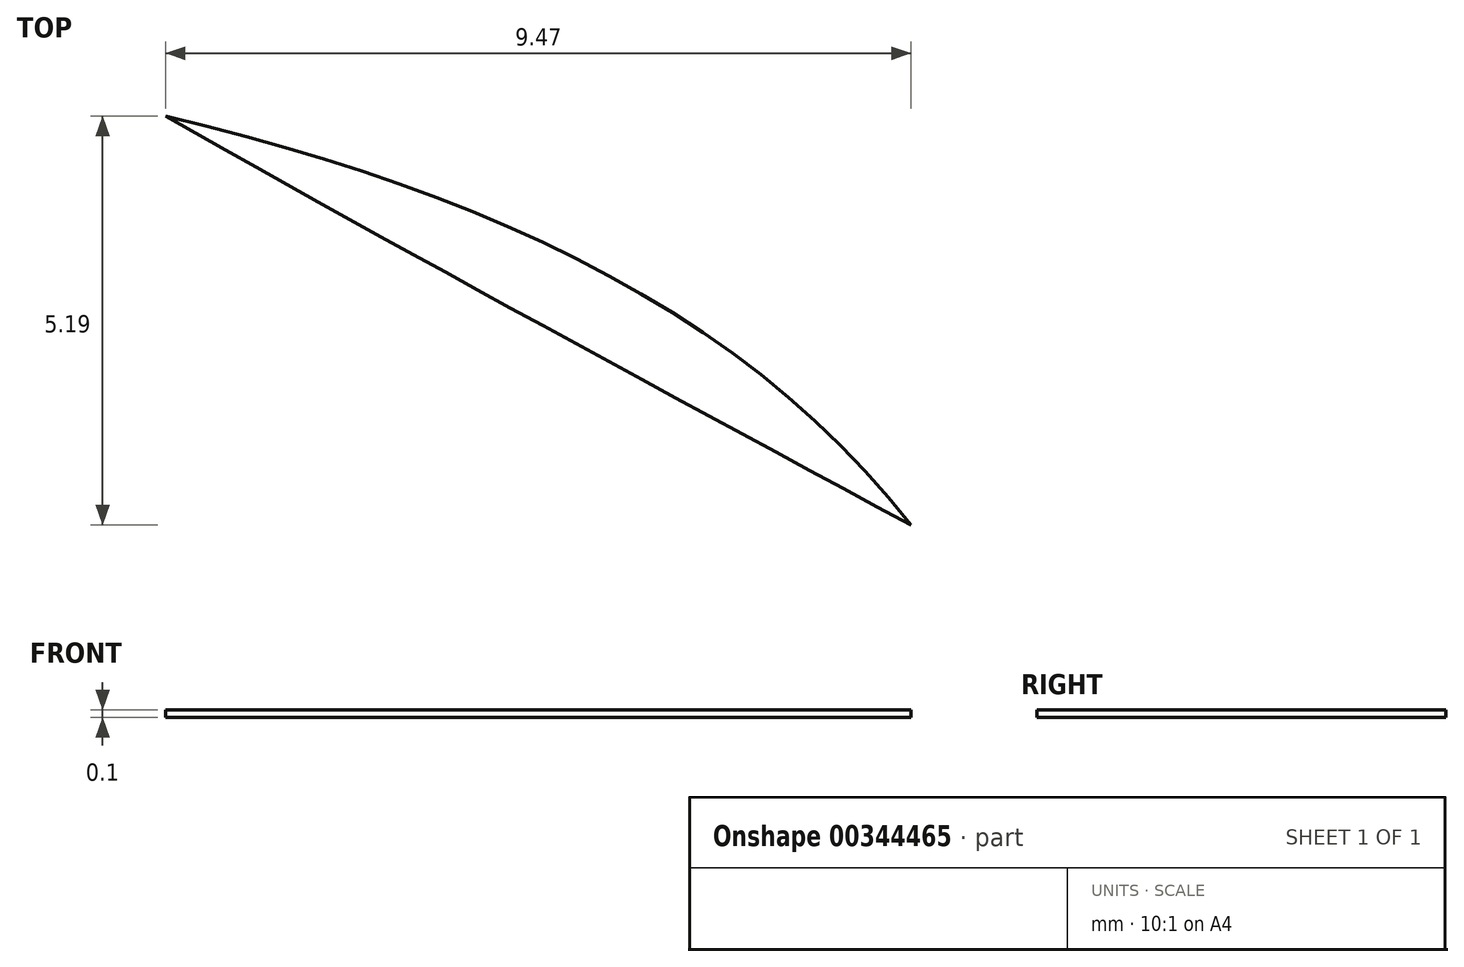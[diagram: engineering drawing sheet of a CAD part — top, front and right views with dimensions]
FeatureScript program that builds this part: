
annotation { "Feature Type Name" : "Feature", "Feature Type Description" : "" }
export const myFeature = defineFeature(function(context is Context, id is Id, definition is map)
    precondition{}
    {
        {
            var Q0;
            Q0=qCreatedBy(makeId("Top.planeOp"),FACE);
            var sketch = newSketch(context, id + "F0", { "sketchPlane" : qUnion([Q0])});
            skCircle(sketch, "E0", {"center": v(-15.45, 15.45) * mm, "radius": 1.5 * mm});
            skCircle(sketch, "E1.MirrorC", {"center": v(15.45, 15.45) * mm, "radius": 1.5 * mm});
            skCircle(sketch, "E2.MirrorC", {"center": v(-15.45, -15.45) * mm, "radius": 1.5 * mm});
            skCircle(sketch, "E3.MirrorC", {"center": v(15.45, -15.45) * mm, "radius": 1.5 * mm});
            skFitSpline(sketch, "E4", {"points": [v(-18, 21.97) * mm, v(-40.78, 23.07) * mm, v(-21.8, 10.59) * mm], "startDerivative": vector(-66.4, 9) * mm, "endDerivative": vector(58.84, -31.77) * mm});
            skFitSpline(sketch, "E5", {"points": [v(-20.03, -19.63) * mm, v(-30, -40.14) * mm, v(-11, -27.53) * mm], "startDerivative": vector(-34.44, -57.57) * mm, "endDerivative": vector(52.5, 41.76) * mm});
            skFitSpline(sketch, "E6", {"points": [v(-20.03, -19.63) * mm, v(-21.8, 10.59) * mm, v(-42.63, 17.36) * mm], "startDerivative": vector(8.08, 67.05) * mm, "endDerivative": vector(-54.98, 5.27) * mm});
            skPoint(sketch, "E7.orphan", {"position": v(-38.92, 28.77) * mm});
            skPoint(sketch, "E8.start.orphan", {"position": v(-21.8, 0) * mm});
            skPoint(sketch, "E9.orphan", {"position": v(-34.52, -36.18) * mm});
            skFitSpline(sketch, "E10", {"points": [v(-18, 21.97) * mm, v(-4.5, 47) * mm, v(0, 47) * mm, v(4.5, 47) * mm, v(18, 21.97) * mm], "startDerivative": vector(39.93, 96.92) * mm, "endDerivative": vector(39.93, -96.92) * mm});
            skPoint(sketch, "E11.start.orphan", {"position": v(-9, 47) * mm});
            skPoint(sketch, "E12.MirrorCS.start.orphan", {"position": v(9, 47) * mm});
            skPoint(sketch, "E13.MirrorP", {"position": v(34.52, -36.18) * mm});
            skFitSpline(sketch, "E14.MirrorCS", {"points": [v(18, 21.97) * mm, v(4.5, 47) * mm, v(0, 47) * mm, v(-4.5, 47) * mm, v(-18, 21.97) * mm], "startDerivative": vector(-39.93, 96.92) * mm, "endDerivative": vector(-39.93, -96.92) * mm});
            skFitSpline(sketch, "E15.MirrorCS", {"points": [v(18, 21.97) * mm, v(40.78, 23.07) * mm, v(21.8, 10.59) * mm], "startDerivative": vector(66.4, 9) * mm, "endDerivative": vector(-58.84, -31.77) * mm});
            skPoint(sketch, "E16.MirrorP", {"position": v(38.92, 28.77) * mm});
            skFitSpline(sketch, "E17.MirrorCS", {"points": [v(20.03, -19.63) * mm, v(30, -40.14) * mm, v(11, -27.53) * mm], "startDerivative": vector(34.44, -57.57) * mm, "endDerivative": vector(-52.5, 41.76) * mm});
            skFitSpline(sketch, "E18.MirrorCS", {"points": [v(20.03, -19.63) * mm, v(21.8, 10.59) * mm, v(42.63, 17.36) * mm], "startDerivative": vector(-8.08, 67.05) * mm, "endDerivative": vector(54.98, 5.27) * mm});
            skPoint(sketch, "E19.MirrorP", {"position": v(21.8, 0) * mm});
            skPoint(sketch, "E20.end.orphan", {"position": v(-25.49, -44.09) * mm});
            skPoint(sketch, "E21.MirrorCS.end.orphan", {"position": v(25.49, -44.09) * mm});
            skFitSpline(sketch, "E22", {"points": [v(-11, -27.53) * mm, v(-5.5, -27.53) * mm, v(0, -23.83) * mm, v(5.5, -27.53) * mm, v(11, -27.53) * mm], "startDerivative": vector(23.57, -5.82) * mm, "endDerivative": vector(23.57, 5.82) * mm});
            skPoint(sketch, "E23.orphan", {"position": v(0, -27.53) * mm});
            skFitSpline(sketch, "E24", {"points": [v(0, 42.52) * mm, v(-6.2, 33.26) * mm, v(-8.92, 26.18) * mm, v(-3.65, 17.1) * mm, v(-10.37, -21.52) * mm, v(0, -9.67) * mm], "startDerivative": vector(-36.66, -54.14) * mm, "endDerivative": vector(73.8, 101.21) * mm});
            skLineSegment(sketch, "E25", {"start": v(-12.18, 20.81) * mm, "end": v(-12.32, 20.58) * mm});
            skPoint(sketch, "E26.3.internal.snap0", {"position": v(-12.18, 20.81) * mm});
            skFitSpline(sketch, "E26", {"points": [v(-12.18, 20.81) * mm, v(-8.56, 16.83) * mm, v(-13.13, -11.62) * mm, v(-12.18, 0) * mm, v(-11.23, 14.55) * mm, v(-12.18, 20.81) * mm]});
            skFitSpline(sketch, "E27.MirrorC", {"points": [v(12.18, 20.81) * mm, v(8.56, 16.83) * mm, v(13.13, -11.62) * mm, v(12.18, 0) * mm, v(11.23, 14.55) * mm, v(12.18, 20.81) * mm]});
            skFitSpline(sketch, "E28.MirrorCS", {"points": [v(0, 42.52) * mm, v(6.2, 33.26) * mm, v(8.92, 26.18) * mm, v(3.65, 17.1) * mm, v(10.37, -21.52) * mm, v(0, -9.67) * mm], "startDerivative": vector(36.66, -54.14) * mm, "endDerivative": vector(-73.8, 101.21) * mm});
            skLineSegment(sketch, "E29.MirrorCS", {"start": v(12.18, 20.81) * mm, "end": v(12.32, 20.58) * mm});
            skFitSpline(sketch, "E30", {"points": [v(-5, -16.51) * mm, v(0, -12.78) * mm, v(5, -16.51) * mm], "startDerivative": vector(8.9, 11.91) * mm, "endDerivative": vector(9.7, -11.27) * mm});
            skLineSegment(sketch, "E31", {"start": v(0, -23.83) * mm, "end": v(0, 47) * mm, "construction": true});
            skCircle(sketch, "E32", {"center": v(-16.5, 20) * mm, "radius": 1.5 * mm});
            skCircle(sketch, "E33.MirrorC", {"center": v(16.5, 20) * mm, "radius": 1.5 * mm});
            skCircle(sketch, "E34", {"center": v(-16.5, -41) * mm, "radius": 1.5 * mm});
            skCircle(sketch, "E35.MirrorC", {"center": v(16.5, -41) * mm, "radius": 1.5 * mm});
            skSolve(sketch);
        }
        {
            var Q0;
            Q0=makeQuery(id+"F0.imprint","IMPRINT",FACE,{"disambiguationData":[TD([[makeQuery(id+"F0.imprint","IMPRINT",EDGE,{"derivedFrom":sQuery(id+"F0.wireOp",EDGE,"E4")}),1.0]])]});
            extrude(context, id + "F1", {"entities" : qUnion([Q0]), "depth" : 0.1 * mm});
        }
    });
